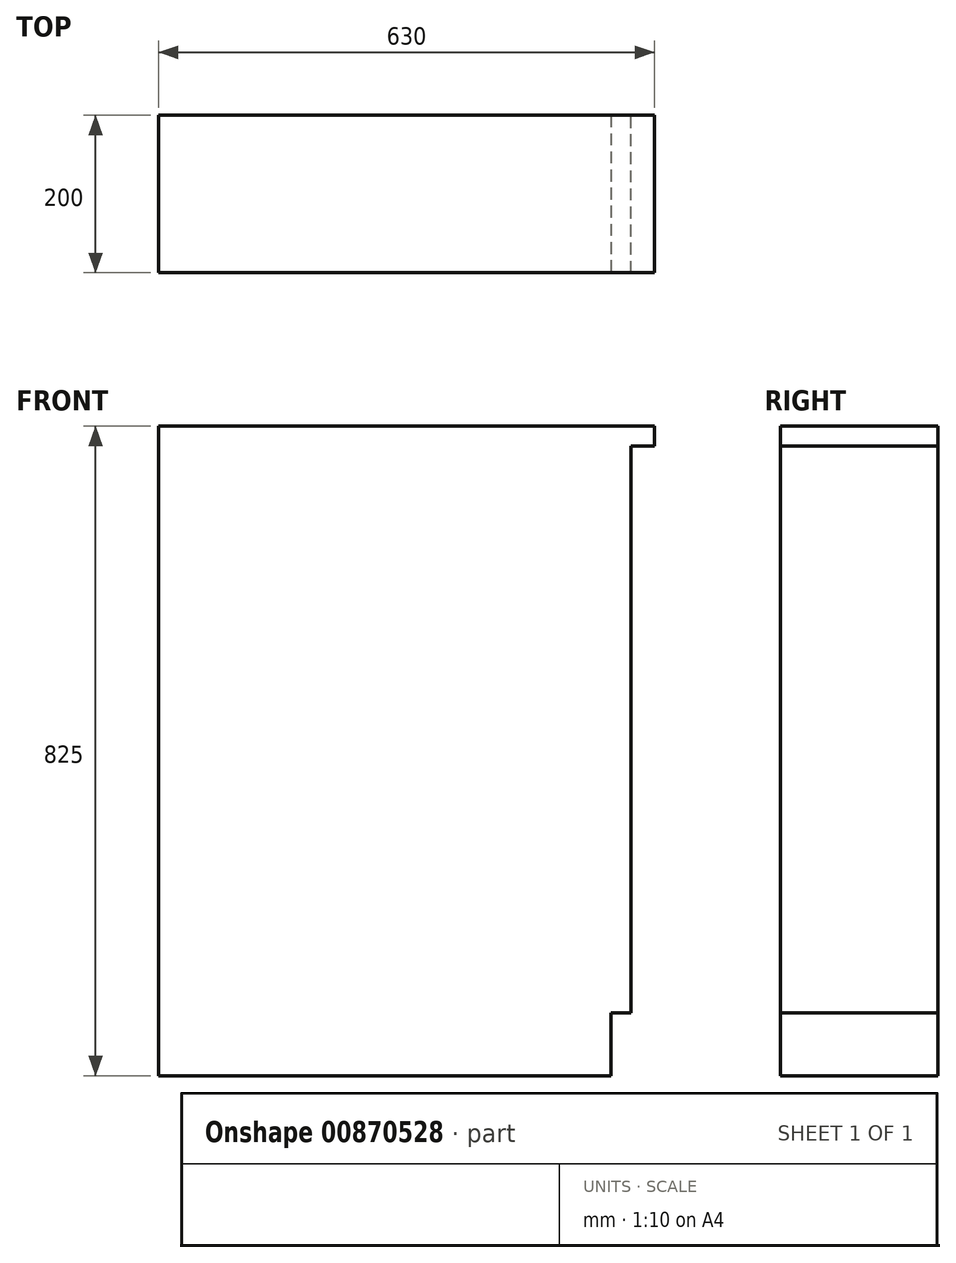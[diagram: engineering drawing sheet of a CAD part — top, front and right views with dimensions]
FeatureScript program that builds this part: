
annotation { "Feature Type Name" : "Feature", "Feature Type Description" : "" }
export const myFeature = defineFeature(function(context is Context, id is Id, definition is map)
    precondition{}
    {
        {
            var Q0;
            Q0=qCreatedBy(makeId("Top.planeOp"),FACE);
            var sketch = newSketch(context, id + "F0", { "sketchPlane" : qUnion([Q0])});
            skLineSegment(sketch, "E0.bottom", {"start": v(-300, 100) * mm, "end": v(300, 100) * mm});
            skLineSegment(sketch, "E0.top", {"start": v(-300, -100) * mm, "end": v(300, -100) * mm});
            skLineSegment(sketch, "E0.left", {"start": v(-300, 100) * mm, "end": v(-300, -100) * mm});
            skLineSegment(sketch, "E0.right", {"start": v(300, 100) * mm, "end": v(300, -100) * mm});
            skPoint(sketch, "E0.middle", {"position": v(0, 0) * mm});
            skSolve(sketch);
        }
        {
            var Q0;
            Q0=qSketchRegion(id+"F0",true);
            extrude(context, id + "F1", {"entities" : qUnion([Q0]), "depth" : 800 * mm, "offsetDistance" : 25 * mm});
        }
        {
            var Q0;
            Q0=makeQuery(id+"F1.opExtrude","SWEPT_FACE",FACE,{"disambiguationData":[OSD([sQuery(id+"F0.wireOp",EDGE,"E0.right")])]});
            var sketch = newSketch(context, id + "F2", { "sketchPlane" : qUnion([Q0])});
            skLineSegment(sketch, "E1.bottom", {"start": v(-100, 0) * mm, "end": v(100, 0) * mm});
            skLineSegment(sketch, "E1.top", {"start": v(-100, 80) * mm, "end": v(100, 80) * mm});
            skLineSegment(sketch, "E1.left", {"start": v(-100, 0) * mm, "end": v(-100, 80) * mm});
            skLineSegment(sketch, "E1.right", {"start": v(100, 0) * mm, "end": v(100, 80) * mm});
            skSolve(sketch);
        }
        {
            var Q0;
            Q0=qSketchRegion(id+"F2",true);
            extrude(context, id + "F3", {"entities" : qUnion([Q0]), "operationType" : NewBodyOperationType.REMOVE, "oppositeDirection" : true, "depth" : 25 * mm, "offsetDistance" : 25 * mm});
        }
        {
            var Q0;
            Q0=makeQuery(id+"F1.opExtrude","CAP_FACE",FACE,{"disambiguationData":[OSD([sQuery(id+"F0.wireOp",EDGE,"E0.bottom"),sQuery(id+"F0.wireOp",EDGE,"E0.top"),sQuery(id+"F0.wireOp",EDGE,"E0.left"),sQuery(id+"F0.wireOp",EDGE,"E0.right")])],"isStart":false});
            var sketch = newSketch(context, id + "F4", { "sketchPlane" : qUnion([Q0])});
            skLineSegment(sketch, "E2.bottom", {"start": v(-300, -100) * mm, "end": v(330, -100) * mm});
            skLineSegment(sketch, "E2.top", {"start": v(-300, 100) * mm, "end": v(330, 100) * mm});
            skLineSegment(sketch, "E2.left", {"start": v(-300, -100) * mm, "end": v(-300, 100) * mm});
            skLineSegment(sketch, "E2.right", {"start": v(330, -100) * mm, "end": v(330, 100) * mm});
            skSolve(sketch);
        }
        {
            var Q0;
            Q0=qSketchRegion(id+"F4",true);
            extrude(context, id + "F5", {"entities" : qUnion([Q0]), "operationType" : NewBodyOperationType.ADD, "depth" : 25 * mm, "offsetDistance" : 25 * mm});
        }
    });
